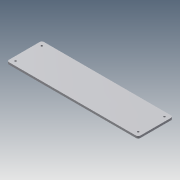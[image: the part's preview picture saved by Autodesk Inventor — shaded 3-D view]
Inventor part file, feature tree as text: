
AUTODESK INVENTOR PART (.ipt)
format: ipt  version: 2014 (Build 180170000, 170)  size: 100,864 bytes
history: native  units: mm
features: extrude x2, sketch x2, fillet x1
ambient origin geometry x8: Origin, YZ Plane, XZ Plane, XY Plane, X Axis, Y Axis, Z Axis, Center Point
bodies: Solid1 (feature_tree)
feature tree (5):
  extrude  "Extrusion1"  Depth=100.0mm
  extrude  "Extrusion8"  Depth=6.0mm
  fillet  "Fillet3"  Radius=10.0mm
  sketch  "Sketch1"  dims[d0=375.0mm d1=100.0mm]
  sketch  "Sketch8"  dims[d2=6.0mm d3=0.0mm d30=6.0mm d38=10.0mm d39=0.0mm d40=12.5mm d41=12.5mm d42=12.5mm d43=12.5mm d44=5.4mm]
